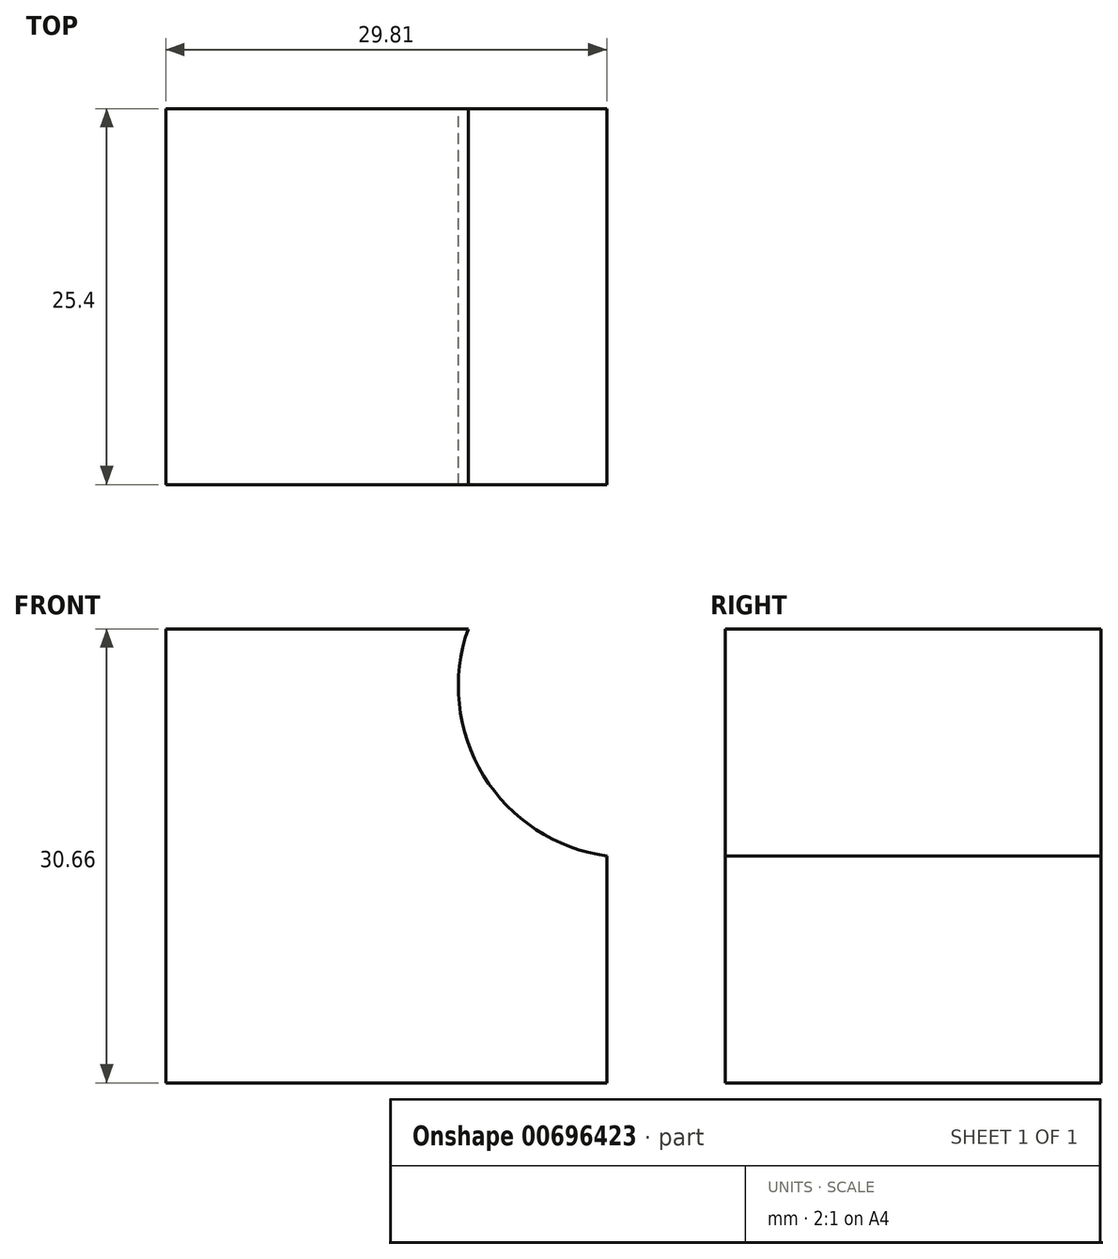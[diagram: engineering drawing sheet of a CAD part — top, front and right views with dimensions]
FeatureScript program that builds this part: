
annotation { "Feature Type Name" : "Feature", "Feature Type Description" : "" }
export const myFeature = defineFeature(function(context is Context, id is Id, definition is map)
    precondition{}
    {
        {
            var Q0;
            Q0=qCreatedBy(makeId("Front.planeOp"),FACE);
            var sketch = newSketch(context, id + "F0", { "sketchPlane" : qUnion([Q0])});
            skLineSegment(sketch, "E0.bottom", {"start": v(-52.27, 39.39) * mm, "end": v(-31.83, 39.39) * mm});
            skLineSegment(sketch, "E0.top", {"start": v(-52.27, 8.73) * mm, "end": v(-22.46, 8.73) * mm});
            skLineSegment(sketch, "E0.left", {"start": v(-52.27, 39.39) * mm, "end": v(-52.27, 8.73) * mm});
            skLineSegment(sketch, "E0.right", {"start": v(-22.46, 24.06) * mm, "end": v(-22.46, 8.73) * mm});
            skArc(sketch, "E1", {"start": v(-31.83, 39.39) * mm, "mid": v(-30.8, 29.5) * mm, "end": v(-22.46, 24.06) * mm});
            skPoint(sketch, "E2.orphan", {"position": v(-22.46, 39.39) * mm});
            skSolve(sketch);
        }
        {
            var Q0;
            Q0=makeQuery(id+"F0.imprint","IMPRINT",FACE,{"disambiguationData":[TD([[makeQuery(id+"F0.imprint","IMPRINT",EDGE,{"derivedFrom":sQuery(id+"F0.wireOp",EDGE,"E0.bottom")}),-1.0]])]});
            extrude(context, id + "F1", {"entities" : qUnion([Q0]), "depth" : 25.4 * mm, "offsetDistance" : 25.4 * mm});
        }
    });
